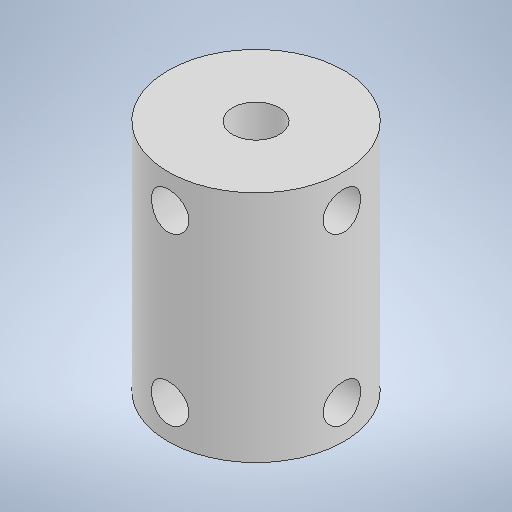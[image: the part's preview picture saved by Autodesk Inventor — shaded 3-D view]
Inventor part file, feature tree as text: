
AUTODESK INVENTOR PART (.ipt)
format: ipt  version: 2025.2 (Build 292293000, 293)  size: 242,688 bytes
history: native  units: mm
features: extrude x3, sketch x2, plane x1, pattern_circular x1
ambient origin geometry x8: Origin, YZ Plane, XZ Plane, XY Plane, X Axis, Y Axis, Z Axis, Center Point
bodies: Solid1 (feature_tree)
feature tree (7):
  sketch  "Sketch1"  dims[d0=8.0mm d1=18.8mm]
  extrude  "Extrusion1"  Depth=18.8mm
  extrude  "Extrusion2"  Depth=25.0mm TaperAngle=0.0deg
  plane  "Work Plane1"
  extrude  "Extrusion3"  Depth=18.5mm TaperAngle=0.0deg
  pattern_circular  "Circular Pattern1"  [2 undecoded]
  sketch  "Sketch2"  dims[d2=5.0mm d3=25.0mm d4=0.0mm d5=18.5mm d6=0.0mm d7=4.0mm d8=3.6mm d9=3.6mm d10=18.8mm d11=0.0mm d12=20.0mm d13=90.0deg]
note: 2 required parameter values undecoded (feature->parameter linkage not recoverable at this tier; creation-order binding heuristic only, values carry confidence <= 0.55)
